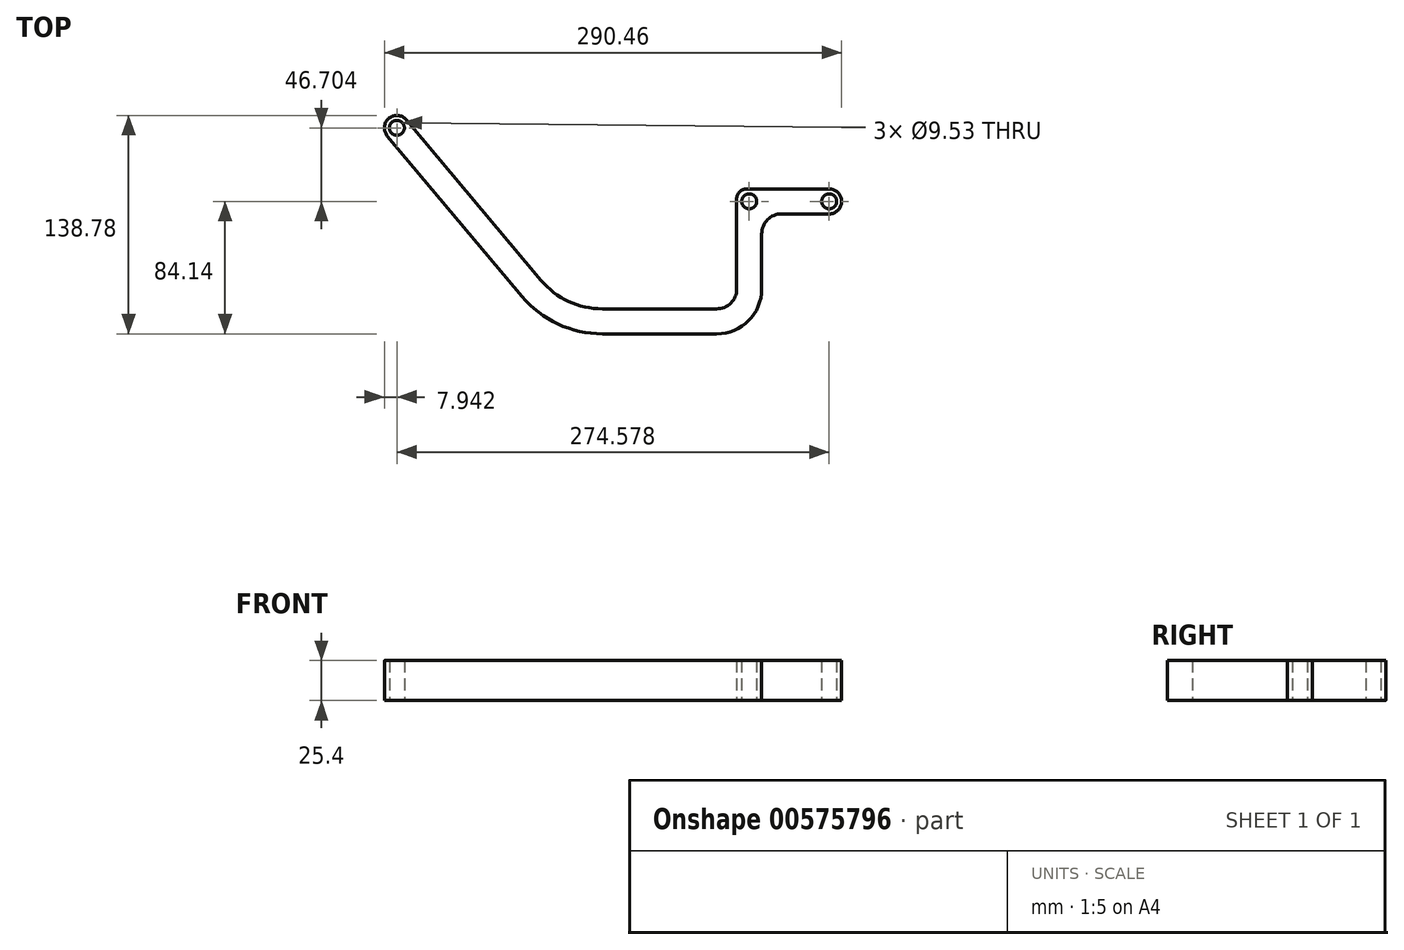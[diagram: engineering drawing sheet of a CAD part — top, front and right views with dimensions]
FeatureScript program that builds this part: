
annotation { "Feature Type Name" : "Feature", "Feature Type Description" : "" }
export const myFeature = defineFeature(function(context is Context, id is Id, definition is map)
    precondition{}
    {
        {
            var Q0;
            Q0=qCreatedBy(makeId("Top.planeOp"),FACE);
            var sketch = newSketch(context, id + "F0", { "sketchPlane" : qUnion([Q0])});
            skLineSegment(sketch, "E0", {"start": v(0, 0) * mm, "end": v(-50.8, 0) * mm});
            skLineSegment(sketch, "E1", {"start": v(-50.8, 0) * mm, "end": v(-50.8, -76.2) * mm});
            skLineSegment(sketch, "E2", {"start": v(-50.8, -76.2) * mm, "end": v(-171.45, -76.2) * mm});
            skLineSegment(sketch, "E3", {"start": v(-171.45, -76.2) * mm, "end": v(-274.58, 46.7) * mm});
            skSolve(sketch);
        }
        {
            var Q0;
            Q0=qCreatedBy(makeId("Top.planeOp"),FACE);
            var sketch = newSketch(context, id + "F1", { "sketchPlane" : qUnion([Q0])});
            skLineSegment(sketch, "E4.0", {"start": v(-182.98, -50.12) * mm, "end": v(-268.5, 51.8) * mm});
            skLineSegment(sketch, "E4.1", {"start": v(-71.44, -68.26) * mm, "end": v(-144.06, -68.26) * mm});
            skLineSegment(sketch, "E4.2", {"start": v(-58.74, 1.59) * mm, "end": v(-58.74, -55.56) * mm});
            skLineSegment(sketch, "E4.3", {"start": v(0, 7.94) * mm, "end": v(-52.39, 7.94) * mm});
            skLineSegment(sketch, "E5.0", {"start": v(-195.14, -60.32) * mm, "end": v(-280.66, 41.6) * mm});
            skLineSegment(sketch, "E5.1", {"start": v(-71.44, -84.14) * mm, "end": v(-144.06, -84.14) * mm});
            skLineSegment(sketch, "E5.2", {"start": v(-42.86, -20.64) * mm, "end": v(-42.86, -55.56) * mm});
            skLineSegment(sketch, "E5.3", {"start": v(0, -7.94) * mm, "end": v(-30.16, -7.94) * mm});
            skPoint(sketch, "E6.0", {"position": v(-274.58, 46.7) * mm});
            skPoint(sketch, "E7.0", {"position": v(0, 0) * mm});
            skArc(sketch, "E8", {"start": v(-268.5, 51.8) * mm, "mid": v(-279.68, 52.78) * mm, "end": v(-280.66, 41.6) * mm});
            skCircle(sketch, "E9", {"center": v(0, 0) * mm, "radius": 7.94 * mm});
            skPoint(sketch, "E10.visualSharp", {"position": v(-167.75, -68.26) * mm});
            skArc(sketch, "E10.filletArc", {"start": v(-182.98, -50.12) * mm, "mid": v(-165.53, -63.5) * mm, "end": v(-144.06, -68.26) * mm});
            skPoint(sketch, "E11.visualSharp", {"position": v(-175.15, -84.14) * mm});
            skArc(sketch, "E11.filletArc", {"start": v(-195.14, -60.32) * mm, "mid": v(-172.24, -77.9) * mm, "end": v(-144.06, -84.14) * mm});
            skPoint(sketch, "E12.visualSharp", {"position": v(-58.74, -68.26) * mm});
            skArc(sketch, "E12.filletArc", {"start": v(-71.44, -68.26) * mm, "mid": v(-62.46, -64.54) * mm, "end": v(-58.74, -55.56) * mm});
            skPoint(sketch, "E13.visualSharp", {"position": v(-42.86, -84.14) * mm});
            skArc(sketch, "E13.filletArc", {"start": v(-71.44, -84.14) * mm, "mid": v(-51.23, -75.77) * mm, "end": v(-42.86, -55.56) * mm});
            skPoint(sketch, "E14.visualSharp", {"position": v(-42.86, -7.94) * mm});
            skArc(sketch, "E14.filletArc", {"start": v(-30.16, -7.94) * mm, "mid": v(-39.14, -11.66) * mm, "end": v(-42.86, -20.64) * mm});
            skPoint(sketch, "E15.visualSharp", {"position": v(-58.74, 7.94) * mm});
            skArc(sketch, "E15.filletArc", {"start": v(-52.39, 7.94) * mm, "mid": v(-56.88, 6.08) * mm, "end": v(-58.74, 1.59) * mm});
            skSolve(sketch);
        }
        {
            var Q0;
            {var subQ0=sQuery(id+"F1.wireOp",EDGE,"E9");var subQ1=makeQuery(id+"F1.imprint","INTERSECT",VERTEX,{"derivedFrom":[sQuery(id+"F1.wireOp",EDGE,"E4.3"),subQ0]});Q0=makeQuery(id+"F1.imprint","IMPRINT",FACE,{"disambiguationData":[TD([[makeQuery(id+"F1.imprint","IMPRINT",EDGE,{"disambiguationData":[TD([[subQ1,-1.0]])],"derivedFrom":subQ0}),1.0]])]});}
            var Q1;
            Q1=makeQuery(id+"F1.imprint","IMPRINT",FACE,{"disambiguationData":[TD([[makeQuery(id+"F1.imprint","IMPRINT",EDGE,{"derivedFrom":sQuery(id+"F1.wireOp",EDGE,"E4.0")}),1.0]])]});
            extrude(context, id + "F2", {"entities" : qUnion([Q0, Q1]), "depth" : 25.4 * mm, "offsetDistance" : 25.4 * mm});
        }
        {
            var Q0;
            Q0=sQuery(id+"F0.wireOp",VERTEX,"E3.end");
            var Q1;
            Q1=sQuery(id+"F0.wireOp",VERTEX,"E0.start");
            var Q2;
            Q2=sQuery(id+"F0.wireOp",VERTEX,"E1.start");
            var Q3;
            Q3=makeQuery(id+"F2.opExtrude","SWEPT_BODY",BODY,{"disambiguationData":[OSD([sQuery(id+"F1.wireOp",EDGE,"E4.0"),sQuery(id+"F1.wireOp",EDGE,"E4.1"),sQuery(id+"F1.wireOp",EDGE,"E4.2"),sQuery(id+"F1.wireOp",EDGE,"E4.3"),sQuery(id+"F1.wireOp",EDGE,"E5.0"),sQuery(id+"F1.wireOp",EDGE,"E5.1"),sQuery(id+"F1.wireOp",EDGE,"E5.2"),sQuery(id+"F1.wireOp",EDGE,"E5.3"),sQuery(id+"F1.wireOp",EDGE,"E8"),sQuery(id+"F1.wireOp",EDGE,"E9"),sQuery(id+"F1.wireOp",EDGE,"E10.filletArc"),sQuery(id+"F1.wireOp",EDGE,"E11.filletArc"),sQuery(id+"F1.wireOp",EDGE,"E12.filletArc"),sQuery(id+"F1.wireOp",EDGE,"E13.filletArc"),sQuery(id+"F1.wireOp",EDGE,"E14.filletArc"),sQuery(id+"F1.wireOp",EDGE,"E15.filletArc")])]});
            hole(context, id + "F3", {"style" : HoleStyle.SIMPLE, "endStyle" : HoleEndStyle.THROUGH, "oppositeDirection" : true, "holeDiameter" : 9.52 * mm, "isTappedThrough" : true, "tappedDepth" : 12.7 * mm, "tapClearance" : 3, "locations" : qUnion([Q0, Q1, Q2]), "scope" : qUnion([Q3])});
        }
    });
